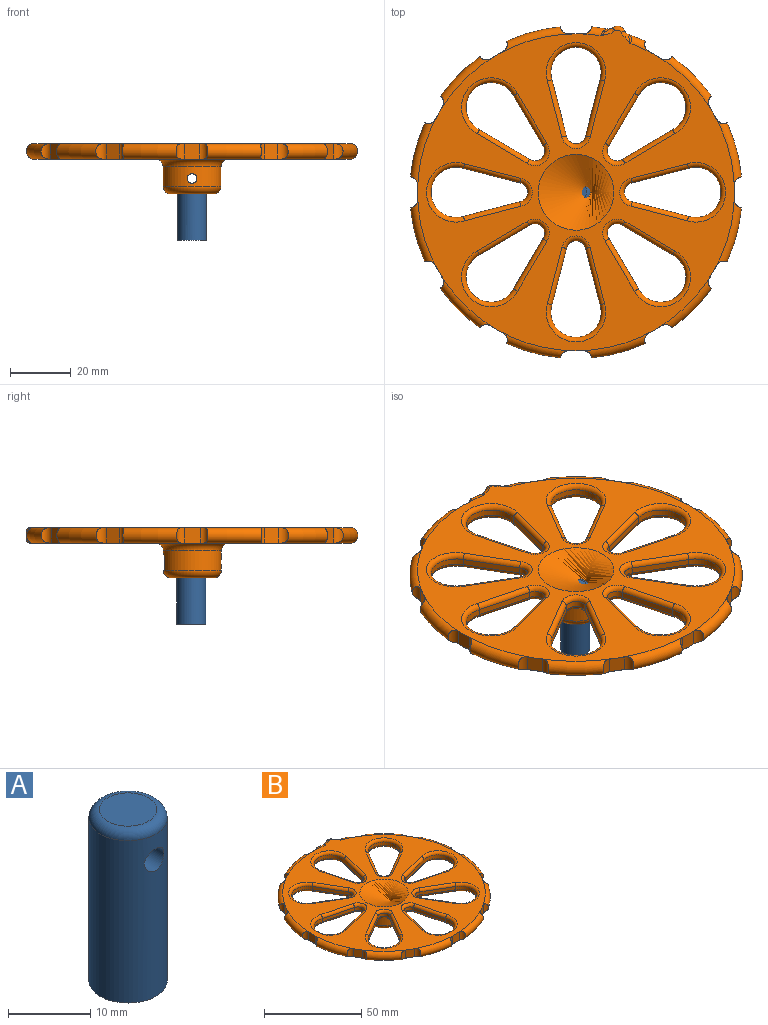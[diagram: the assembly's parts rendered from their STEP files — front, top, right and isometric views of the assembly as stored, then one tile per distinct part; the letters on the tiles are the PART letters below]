
ASSEMBLY  parts=2 mates=1
PART A: 5 faces, bbox 10.3x10.3x25.4 mm
  f0: cylinder r=4.76mm len=24.13mm, axis (0,0,1), area 704.7mm2, adj f1,f3,f4
  f1: plane 9.53x9.53mm, normal (0,0,-1), area 71.3mm2, adj f0
  f2: plane 6.99x6.99mm, normal (0,0,1), area 38.3mm2, adj f4
  f3: cylinder r=1.65mm len=9.53mm, axis (0,-1,0), area 95.8mm2, adj f0
  f4: torus R=3.49mm, axis (0,0,1), area 53.9mm2, adj f0,f2
PART B: 166 faces, bbox 119.8x119.8x20.6 mm
  f0: torus R=52.07mm, axis (0,0,1), area 34.5mm2, adj f16,f18,f31,f54,f158
  f1: torus R=52.07mm, axis (0,0,1), area 41.9mm2, adj f16,f18,f30,f33,f159
  f2: cylinder r=1.59mm len=3.18mm, axis (0,-1,0), area 27.9mm2, adj f15,f155
  f3: torus R=52.07mm, axis (0,0,1), area 151mm2, adj f16,f18,f27,f31,f53,f55
  f4: torus R=52.07mm, axis (0,0,1), area 151mm2, adj f16,f18,f29,f30,f32,f35
  f5: torus R=52.07mm, axis (0,0,1), area 151mm2, adj f16,f18,f28,f29,f34,f37
  f6: torus R=52.07mm, axis (0,0,1), area 151mm2, adj f16,f18,f20,f28,f36,f39
  f7: torus R=52.07mm, axis (0,0,1), area 151mm2, adj f16,f18,f26,f27,f50,f52
  f8: torus R=52.07mm, axis (0,0,1), area 151mm2, adj f16,f18,f25,f26,f48,f51
  f9: torus R=52.07mm, axis (0,0,1), area 151mm2, adj f16,f18,f24,f25,f46,f49
  f10: torus R=52.07mm, axis (0,0,1), area 151mm2, adj f16,f18,f23,f24,f44,f47
  f11: torus R=52.07mm, axis (0,0,1), area 151mm2, adj f16,f18,f22,f23,f42,f45
  f12: torus R=52.07mm, axis (0,0,1), area 151mm2, adj f16,f18,f21,f22,f40,f43
  f13: torus R=52.07mm, axis (0,0,1), area 151mm2, adj f16,f18,f20,f21,f38,f41
  f14: cylinder r=9.53mm len=19.05mm, axis (0,0,-1), area 341.8mm2, adj f56,f57,f58,f156
  f15: cylinder r=4.83mm len=9.65mm, axis (0,0,-1), area 253.5mm2, adj f2,f17,f19,f56
  f16: plane 106.94x105.7mm, normal (0,0,1), area 4140.9mm2, adj f0,f1,f3,f4,f5,f6,f7,f8
  f17: plane 13.97x13.97mm, normal (0,0,-1), area 80.1mm2, adj f15,f57
  f18: plane 106.94x105.7mm, normal (0,0,-1), area 4170.3mm2, adj f0,f1,f3,f4,f5,f6,f7,f8
  f19: torus R=12.45mm, axis (0,0,1), area 571.2mm2, adj f15,f16
  f20: plane 5.11x4.43mm, normal (0.87,-0.5,0), area 25.8mm2, adj f6,f13,f38,f39
  f21: plane 5.11x4.43mm, normal (0.5,-0.87,0), area 25.8mm2, adj f12,f13,f40,f41
  f22: plane 5.11x5.11mm, normal (0,-1,0), area 25.8mm2, adj f11,f12,f42,f43
  f23: plane 5.11x4.43mm, normal (-0.5,-0.87,0), area 25.8mm2, adj f10,f11,f44,f45
  f24: plane 5.11x4.43mm, normal (-0.87,-0.5,0), area 25.8mm2, adj f9,f10,f46,f47
  f25: plane 5.11x5.11mm, normal (-1,0,0), area 25.8mm2, adj f8,f9,f48,f49
  f26: plane 5.11x4.43mm, normal (-0.87,0.5,0), area 25.8mm2, adj f7,f8,f50,f51
  f27: plane 5.11x4.43mm, normal (-0.5,0.87,0), area 25.8mm2, adj f3,f7,f52,f53
  f28: plane 5.11x5.11mm, normal (1,0,0), area 25.8mm2, adj f5,f6,f36,f37
  f29: plane 5.11x4.43mm, normal (0.87,0.5,0), area 25.8mm2, adj f4,f5,f34,f35
  f30: plane 5.11x4.43mm, normal (0.5,0.87,0), area 25.8mm2, adj f1,f4,f32,f33
  f31: plane 5.11x5.11mm, normal (0,1,0), area 25.8mm2, adj f0,f3,f54,f55
  f32: cylinder r=2.54mm len=5.08mm, axis (0,0,-1), area 16.1mm2, adj f4,f30
  f33: cylinder r=2.54mm len=5.08mm, axis (0,0,1), area 16.1mm2, adj f1,f30
  f34: cylinder r=2.54mm len=5.08mm, axis (0,0,-1), area 16.1mm2, adj f5,f29
  f35: cylinder r=2.54mm len=5.08mm, axis (0,0,1), area 16.1mm2, adj f4,f29
  f36: cylinder r=2.54mm len=5.08mm, axis (0,0,-1), area 16.1mm2, adj f6,f28
  f37: cylinder r=2.54mm len=5.08mm, axis (0,0,1), area 16.1mm2, adj f5,f28
  f38: cylinder r=2.54mm len=5.08mm, axis (0,0,-1), area 16.1mm2, adj f13,f20
  f39: cylinder r=2.54mm len=5.08mm, axis (0,0,1), area 16.1mm2, adj f6,f20
  f40: cylinder r=2.54mm len=5.08mm, axis (0,0,-1), area 16.1mm2, adj f12,f21
  f41: cylinder r=2.54mm len=5.08mm, axis (0,0,1), area 16.1mm2, adj f13,f21
  f42: cylinder r=2.54mm len=5.08mm, axis (0,0,-1), area 16.1mm2, adj f11,f22
  f43: cylinder r=2.54mm len=5.08mm, axis (0,0,1), area 16.1mm2, adj f12,f22
  f44: cylinder r=2.54mm len=5.08mm, axis (0,0,-1), area 16.1mm2, adj f10,f23
  f45: cylinder r=2.54mm len=5.08mm, axis (0,0,1), area 16.1mm2, adj f11,f23
  f46: cylinder r=2.54mm len=5.08mm, axis (0,0,-1), area 16.1mm2, adj f9,f24
  f47: cylinder r=2.54mm len=5.08mm, axis (0,0,1), area 16.1mm2, adj f10,f24
  f48: cylinder r=2.54mm len=5.08mm, axis (0,0,-1), area 16.1mm2, adj f8,f25
  f49: cylinder r=2.54mm len=5.08mm, axis (0,0,1), area 16.1mm2, adj f9,f25
  f50: cylinder r=2.54mm len=5.08mm, axis (0,0,-1), area 16.1mm2, adj f7,f26
  f51: cylinder r=2.54mm len=5.08mm, axis (0,0,1), area 16.1mm2, adj f8,f26
  f52: cylinder r=2.54mm len=5.08mm, axis (0,0,1), area 16.1mm2, adj f7,f27
  f53: cylinder r=2.54mm len=5.08mm, axis (0,0,-1), area 16.1mm2, adj f3,f27
  f54: cylinder r=2.54mm len=5.08mm, axis (0,0,-1), area 16.1mm2, adj f0,f31
  f55: cylinder r=2.54mm len=5.08mm, axis (0,0,1), area 16.1mm2, adj f3,f31
  f56: cylinder r=1.59mm len=4.7mm, axis (0,-1,0), area 46.9mm2, adj f14,f15
  f57: torus R=6.99mm, axis (0,0,1), area 214mm2, adj f14,f17,f156
  f58: torus R=12.06mm, axis (0,0,1), area 261.9mm2, adj f14,f18
  f59: plane 18.51x4.78mm, normal (0.97,0.25,0), area 38.8mm2, adj f60,f62,f122,f154
  f60: cylinder r=3.17mm len=6.24mm, axis (0,0,1), area 17.9mm2, adj f59,f61,f121,f153
  f61: plane 18.51x4.78mm, normal (-0.97,0.25,0), area 38.8mm2, adj f60,f62,f119,f151
  f62: cylinder r=8.26mm len=16.51mm, axis (0,0,1), area 62.6mm2, adj f59,f61,f120,f152
  f63: cylinder r=8.26mm len=15.53mm, axis (0,0,1), area 62.6mm2, adj f64,f66,f118,f147
  f64: plane 16.47x9.71mm, normal (0.51,0.86,0), area 38.8mm2, adj f63,f65,f117,f148
  f65: cylinder r=3.17mm len=4.97mm, axis (0,0,1), area 17.9mm2, adj f64,f66,f115,f150
  f66: plane 16.47x9.71mm, normal (-0.86,-0.51,0), area 38.8mm2, adj f63,f65,f116,f149
  f67: cylinder r=8.26mm len=16.51mm, axis (0,0,1), area 62.6mm2, adj f68,f70,f114,f144
  f68: plane 18.51x4.78mm, normal (-0.25,0.97,0), area 38.8mm2, adj f67,f69,f113,f146
  f69: cylinder r=3.17mm len=6.24mm, axis (0,0,1), area 17.9mm2, adj f68,f70,f111,f145
  f70: plane 18.51x4.78mm, normal (-0.25,-0.97,0), area 38.8mm2, adj f67,f69,f112,f143
  f71: cylinder r=8.26mm len=15.53mm, axis (0,0,1), area 62.6mm2, adj f72,f74,f110,f140
  f72: plane 16.47x9.71mm, normal (-0.86,0.51,0), area 38.8mm2, adj f71,f73,f109,f142
  f73: cylinder r=3.17mm len=4.97mm, axis (0,0,1), area 17.9mm2, adj f72,f74,f107,f141
  f74: plane 16.47x9.71mm, normal (0.51,-0.86,0), area 38.8mm2, adj f71,f73,f108,f139
  f75: cylinder r=8.26mm len=16.51mm, axis (0,0,1), area 62.6mm2, adj f76,f78,f106,f136
  f76: plane 18.51x4.78mm, normal (-0.97,-0.25,0), area 38.8mm2, adj f75,f77,f105,f138
  f77: cylinder r=3.17mm len=6.24mm, axis (0,0,1), area 17.9mm2, adj f76,f78,f103,f137
  f78: plane 18.51x4.78mm, normal (0.97,-0.25,0), area 38.8mm2, adj f75,f77,f104,f135
  f79: cylinder r=8.26mm len=15.53mm, axis (0,0,1), area 62.6mm2, adj f80,f82,f102,f132
  f80: plane 16.47x9.71mm, normal (-0.51,-0.86,0), area 38.8mm2, adj f79,f81,f101,f134
  f81: cylinder r=3.17mm len=4.97mm, axis (0,0,1), area 17.9mm2, adj f80,f82,f99,f133
  f82: plane 16.47x9.71mm, normal (0.86,0.51,0), area 38.8mm2, adj f79,f81,f100,f131
  f83: cylinder r=8.26mm len=16.51mm, axis (0,0,1), area 62.6mm2, adj f84,f86,f98,f128
  f84: plane 18.51x4.78mm, normal (0.25,-0.97,0), area 38.8mm2, adj f83,f85,f97,f130
  f85: cylinder r=3.17mm len=6.24mm, axis (0,0,1), area 17.9mm2, adj f84,f86,f95,f129
  f86: plane 18.51x4.78mm, normal (0.25,0.97,0), area 38.8mm2, adj f83,f85,f96,f127
  f87: cylinder r=8.26mm len=15.53mm, axis (0,0,1), area 62.6mm2, adj f88,f90,f94,f124
  f88: plane 16.47x9.71mm, normal (0.86,-0.51,0), area 38.8mm2, adj f87,f89,f93,f126
  f89: cylinder r=3.17mm len=4.97mm, axis (0,0,1), area 17.9mm2, adj f88,f90,f91,f125
  f90: plane 16.47x9.71mm, normal (-0.51,0.86,0), area 38.8mm2, adj f87,f89,f92,f123
  f91: torus R=4.7mm, axis (0,0,1), area 24.6mm2, adj f18,f89,f92,f93
  f92: cylinder r=1.52mm len=17.24mm, axis (0.86,0.51,0), area 45.7mm2, adj f18,f90,f91,f94
  f93: cylinder r=1.52mm len=17.24mm, axis (-0.51,-0.86,0), area 45.7mm2, adj f18,f88,f91,f94
  f94: torus R=9.78mm, axis (0,0,1), area 78.6mm2, adj f18,f87,f92,f93
  f95: torus R=4.7mm, axis (0,0,1), area 24.6mm2, adj f18,f85,f96,f97
  f96: cylinder r=1.52mm len=18.89mm, axis (0.97,-0.25,0), area 45.7mm2, adj f18,f86,f95,f98
  f97: cylinder r=1.52mm len=18.89mm, axis (-0.97,-0.25,0), area 45.7mm2, adj f18,f84,f95,f98
  f98: torus R=9.78mm, axis (0,0,1), area 78.6mm2, adj f18,f83,f96,f97
  f99: torus R=4.7mm, axis (0,0,1), area 24.6mm2, adj f18,f81,f100,f101
  f100: cylinder r=1.52mm len=17.24mm, axis (0.51,-0.86,0), area 45.7mm2, adj f18,f82,f99,f102
  f101: cylinder r=1.52mm len=17.24mm, axis (-0.86,0.51,0), area 45.7mm2, adj f18,f80,f99,f102
  f102: torus R=9.78mm, axis (0,0,1), area 78.6mm2, adj f18,f79,f100,f101
  f103: torus R=4.7mm, axis (0,0,1), area 24.6mm2, adj f18,f77,f104,f105
  f104: cylinder r=1.52mm len=18.89mm, axis (-0.25,-0.97,0), area 45.7mm2, adj f18,f78,f103,f106
  f105: cylinder r=1.52mm len=18.89mm, axis (-0.25,0.97,0), area 45.7mm2, adj f18,f76,f103,f106
  f106: torus R=9.78mm, axis (0,0,1), area 78.6mm2, adj f18,f75,f104,f105
  f107: torus R=4.7mm, axis (0,0,1), area 24.6mm2, adj f18,f73,f108,f109
  f108: cylinder r=1.52mm len=17.24mm, axis (-0.86,-0.51,0), area 45.7mm2, adj f18,f74,f107,f110
  f109: cylinder r=1.52mm len=17.24mm, axis (0.51,0.86,0), area 45.7mm2, adj f18,f72,f107,f110
  f110: torus R=9.78mm, axis (0,0,1), area 78.6mm2, adj f18,f71,f108,f109
  f111: torus R=4.7mm, axis (0,0,1), area 24.6mm2, adj f18,f69,f112,f113
  f112: cylinder r=1.52mm len=18.89mm, axis (-0.97,0.25,0), area 45.7mm2, adj f18,f70,f111,f114
  f113: cylinder r=1.52mm len=18.89mm, axis (0.97,0.25,0), area 45.7mm2, adj f18,f68,f111,f114
  f114: torus R=9.78mm, axis (0,0,1), area 78.6mm2, adj f18,f67,f112,f113
  f115: torus R=4.7mm, axis (0,0,1), area 24.6mm2, adj f18,f65,f116,f117
  f116: cylinder r=1.52mm len=17.24mm, axis (-0.51,0.86,0), area 45.7mm2, adj f18,f66,f115,f118
  f117: cylinder r=1.52mm len=17.24mm, axis (0.86,-0.51,0), area 45.7mm2, adj f18,f64,f115,f118
  f118: torus R=9.78mm, axis (0,0,1), area 78.6mm2, adj f18,f63,f116,f117
  f119: cylinder r=1.52mm len=18.89mm, axis (0.25,0.97,0), area 45.7mm2, adj f18,f61,f120,f121
  f120: torus R=9.78mm, axis (0,0,1), area 78.6mm2, adj f18,f62,f119,f122
  f121: torus R=4.7mm, axis (0,0,1), area 24.6mm2, adj f18,f60,f119,f122
  f122: cylinder r=1.52mm len=18.89mm, axis (0.25,-0.97,0), area 45.7mm2, adj f18,f59,f120,f121
  f123: cylinder r=1.52mm len=17.24mm, axis (-0.86,-0.51,0), area 45.7mm2, adj f16,f90,f124,f125
  f124: torus R=9.78mm, axis (0,0,1), area 78.6mm2, adj f16,f87,f123,f126
  f125: torus R=4.7mm, axis (0,0,1), area 24.6mm2, adj f16,f89,f123,f126
  f126: cylinder r=1.52mm len=17.24mm, axis (0.51,0.86,0), area 45.7mm2, adj f16,f88,f124,f125
  f127: cylinder r=1.52mm len=18.89mm, axis (-0.97,0.25,0), area 45.7mm2, adj f16,f86,f128,f129
  f128: torus R=9.78mm, axis (0,0,1), area 78.6mm2, adj f16,f83,f127,f130
  f129: torus R=4.7mm, axis (0,0,1), area 24.6mm2, adj f16,f85,f127,f130
  f130: cylinder r=1.52mm len=18.89mm, axis (0.97,0.25,0), area 45.7mm2, adj f16,f84,f128,f129
  f131: cylinder r=1.52mm len=17.24mm, axis (-0.51,0.86,0), area 45.7mm2, adj f16,f82,f132,f133
  f132: torus R=9.78mm, axis (0,0,1), area 78.6mm2, adj f16,f79,f131,f134
  f133: torus R=4.7mm, axis (0,0,1), area 24.6mm2, adj f16,f81,f131,f134
  f134: cylinder r=1.52mm len=17.24mm, axis (0.86,-0.51,0), area 45.7mm2, adj f16,f80,f132,f133
  f135: cylinder r=1.52mm len=18.89mm, axis (0.25,0.97,0), area 45.7mm2, adj f16,f78,f136,f137
  f136: torus R=9.78mm, axis (0,0,1), area 78.6mm2, adj f16,f75,f135,f138
  f137: torus R=4.7mm, axis (0,0,1), area 24.6mm2, adj f16,f77,f135,f138
  f138: cylinder r=1.52mm len=18.89mm, axis (0.25,-0.97,0), area 45.7mm2, adj f16,f76,f136,f137
  f139: cylinder r=1.52mm len=17.24mm, axis (0.86,0.51,0), area 45.7mm2, adj f16,f74,f140,f141
  f140: torus R=9.78mm, axis (0,0,1), area 78.6mm2, adj f16,f71,f139,f142
  f141: torus R=4.7mm, axis (0,0,1), area 24.6mm2, adj f16,f73,f139,f142
  f142: cylinder r=1.52mm len=17.24mm, axis (-0.51,-0.86,0), area 45.7mm2, adj f16,f72,f140,f141
  f143: cylinder r=1.52mm len=18.89mm, axis (0.97,-0.25,0), area 45.7mm2, adj f16,f70,f144,f145
  f144: torus R=9.78mm, axis (0,0,1), area 78.6mm2, adj f16,f67,f143,f146
  f145: torus R=4.7mm, axis (0,0,1), area 24.6mm2, adj f16,f69,f143,f146
  f146: cylinder r=1.52mm len=18.89mm, axis (-0.97,-0.25,0), area 45.7mm2, adj f16,f68,f144,f145
  f147: torus R=9.78mm, axis (0,0,1), area 78.6mm2, adj f16,f63,f148,f149
  f148: cylinder r=1.52mm len=17.24mm, axis (-0.86,0.51,0), area 45.7mm2, adj f16,f64,f147,f150
  f149: cylinder r=1.52mm len=17.24mm, axis (0.51,-0.86,0), area 45.7mm2, adj f16,f66,f147,f150
  f150: torus R=4.7mm, axis (0,0,1), area 24.6mm2, adj f16,f65,f148,f149
  f151: cylinder r=1.52mm len=18.89mm, axis (-0.25,-0.97,0), area 45.7mm2, adj f16,f61,f152,f153
  f152: torus R=9.78mm, axis (0,0,1), area 78.6mm2, adj f16,f62,f151,f154
  f153: torus R=4.7mm, axis (0,0,1), area 24.6mm2, adj f16,f60,f151,f154
  f154: cylinder r=1.52mm len=18.89mm, axis (-0.25,0.97,0), area 45.7mm2, adj f16,f59,f152,f153
  f155: plane 6.35x6.35mm, normal (0,1,0), area 23.8mm2, adj f2,f156
  f156: cylinder r=3.17mm len=6.35mm, axis (0,1,0), area 35.1mm2, adj f14,f57,f155
  f157: cylinder r=2.54mm len=3.94mm, axis (0,0,1), area 11.6mm2, adj f158,f159,f161,f164
  f158: bspline ~10.17x3.66mm, area 15.7mm2, adj f0,f157,f160,f163
  f159: bspline ~10.17x4.37mm, area 15.7mm2, adj f1,f157,f162,f165
  f160: bspline ~4.89x3.17mm, area 3.2mm2, adj f16,f158,f161
  f161: torus R=1.27mm, axis (0,0,1), area 7.7mm2, adj f16,f157,f160,f162
  f162: bspline ~4.03x2.92mm, area 3.4mm2, adj f16,f159,f161
  f163: bspline ~4.89x3.17mm, area 3.4mm2, adj f18,f158,f164
  f164: torus R=1.27mm, axis (0,0,1), area 7.7mm2, adj f18,f157,f163,f165
  f165: bspline ~4.64x3.18mm, area 3.3mm2, adj f18,f159,f164
PLACE A t=(5.54,4.09,15.43)mm
PLACE B t=(5.54,3.79,5.27)mm
MATE fastened A.f3 <-> B.f2  axis (0,-1,0) through (5.54,-0.73,10.35)mm
